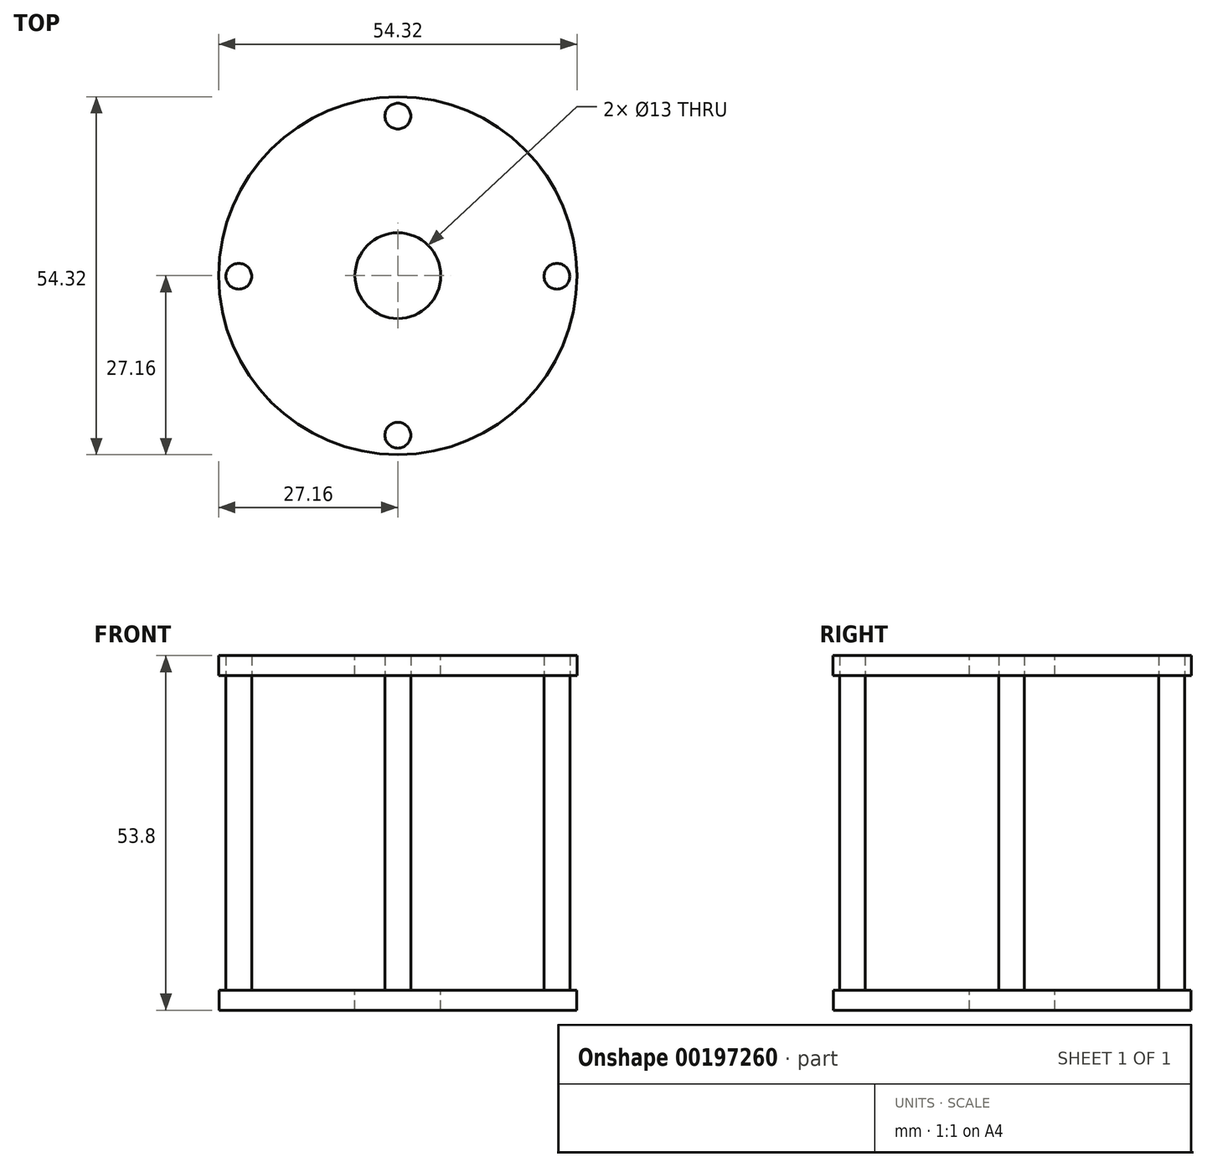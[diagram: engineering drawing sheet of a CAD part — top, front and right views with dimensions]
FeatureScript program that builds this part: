
annotation { "Feature Type Name" : "Feature", "Feature Type Description" : "" }
export const myFeature = defineFeature(function(context is Context, id is Id, definition is map)
    precondition{}
    {
        {
            var Q0;
            Q0=qCreatedBy(makeId("Top.planeOp"),FACE);
            var sketch = newSketch(context, id + "F0", { "sketchPlane" : qUnion([Q0])});
            skCircle(sketch, "E0", {"center": v(0, 0) * mm, "radius": 27.1 * mm});
            skSolve(sketch);
        }
        {
            var Q0;
            Q0 = qSketchRegion(id + "F0", true);
            extrude(context, id + "F1", {"entities" : qUnion([Q0]), "depth" : 3 * mm});
        }
        {
            var Q0;
            Q0=makeQuery(id+"F1.opExtrude","CAP_FACE",FACE,{"disambiguationData":[OSD([sQuery(id+"F0.wireOp",EDGE,"E0")])],"isStart":false});
            var sketch = newSketch(context, id + "F2", { "sketchPlane" : qUnion([Q0])});
            skCircle(sketch, "E1", {"center": v(0, 24.21) * mm, "radius": 1.96 * mm});
            skCircle(sketch, "E2.MirrorC", {"center": v(0, -24.21) * mm, "radius": 1.96 * mm});
            skCircle(sketch, "E3", {"center": v(-24.12, -0.1) * mm, "radius": 1.96 * mm});
            skCircle(sketch, "E4.MirrorC", {"center": v(24.12, -0.1) * mm, "radius": 1.96 * mm});
            skSolve(sketch);
        }
        {
            var Q0;
            Q0 = qSketchRegion(id + "F2", true);
            extrude(context, id + "F3", {"entities" : qUnion([Q0]), "operationType" : NewBodyOperationType.ADD, "depth" : 50.8 * mm});
        }
        {
            var Q0;
            Q0=qCreatedBy(makeId("Top.planeOp"),FACE);
            cPlane(context, id + "F4", {"entities" : qUnion([Q0]), "cplaneType" : CPlaneType.OFFSET, "offset" : 50.8 * mm, "width" : 152.4 * mm, "height" : 152.4 * mm});
        }
        {
            var Q0;
            Q0=qCreatedBy(id+"F4.planeOp",FACE);
            var sketch = newSketch(context, id + "F5", { "sketchPlane" : qUnion([Q0])});
            skCircle(sketch, "E5", {"center": v(0, 0) * mm, "radius": 27.16 * mm});
            skSolve(sketch);
        }
        {
            var Q0;
            Q0=makeQuery(id+"F5.imprint","IMPRINT",FACE,{"disambiguationData":[TD([[makeQuery(id+"F5.imprint","IMPRINT",EDGE,{"derivedFrom":sQuery(id+"F5.wireOp",EDGE,"E5")}),1.0]])]});
            extrude(context, id + "F6", {"entities" : qUnion([Q0]), "depth" : 3 * mm});
        }
        {
            var Q0;
            Q0=makeQuery(id+"F6.opExtrude","CAP_FACE",FACE,{"disambiguationData":[OSD([sQuery(id+"F5.wireOp",EDGE,"E5")])],"isStart":false});
            var sketch = newSketch(context, id + "F7", { "sketchPlane" : qUnion([Q0])});
            skCircle(sketch, "E6", {"center": v(0, 0) * mm, "radius": 6.5 * mm});
            skSolve(sketch);
        }
        {
            var Q0;
            Q0=sQuery(id+"F7.wireOp",VERTEX,"E6.center");
            var Q1;
            Q1=makeQuery(id+"F1.opExtrude","SWEPT_BODY",BODY,{"disambiguationData":[OSD([sQuery(id+"F0.wireOp",EDGE,"E0")])]});
            var Q2;
            Q2=makeQuery(id+"F6.opExtrude","SWEPT_BODY",BODY,{"disambiguationData":[OSD([sQuery(id+"F5.wireOp",EDGE,"E5")])]});
            hole(context, id + "F8", {"style" : HoleStyle.SIMPLE, "endStyle" : HoleEndStyle.THROUGH, "holeDiameter" : 13 * mm, "locations" : qUnion([Q0]), "scope" : qUnion([Q1, Q2]), "isTappedThrough" : true});
        }
    });
